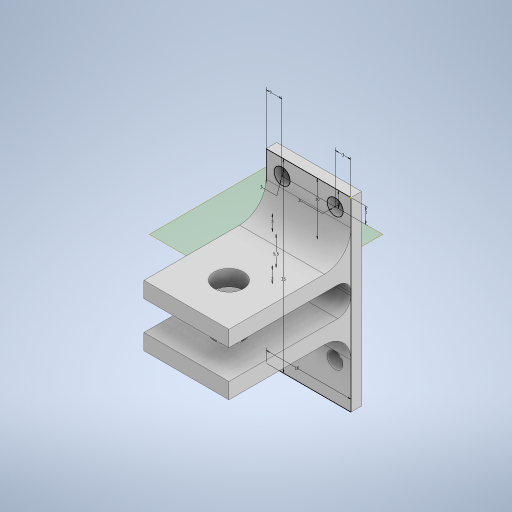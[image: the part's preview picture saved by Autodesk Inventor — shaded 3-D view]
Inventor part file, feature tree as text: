
AUTODESK INVENTOR PART (.ipt)
format: ipt  version: 2024.2 (Build 282272000, 272)  size: 312,832 bytes
history: native  units: mm
features: extrude x5, other x4, sketch x3, fillet x1, projected_geometry x1
ambient origin geometry x8: Origin, YZ Plane, XZ Plane, XY Plane, X Axis, Y Axis, Z Axis, Center Point
bodies: Body1 (feature_tree)
feature tree (14):
  sketch  "Эскиз6"
  extrude  "Выдавливание8"  Depth=16.0mm
  other  "РабПлоскость12"
  sketch  "Эскиз7"
  extrude  "Выдавливание11"  Depth=35.0mm
  extrude  "Выдавливание12"  Depth=3.0mm
  other  "Сопряжение грани1"
  other  "Сопряжение грани2"
  other  "Сопряжение грани3"
  fillet  "Сопряжение1"  Radius=3.0mm
  extrude  "Выдавливание13"  Depth=3.0mm
  extrude  "Выдавливание14"  Depth=3.0mm
  sketch  "Эскиз8"
  projected_geometry  "Спроецированная петля3"
